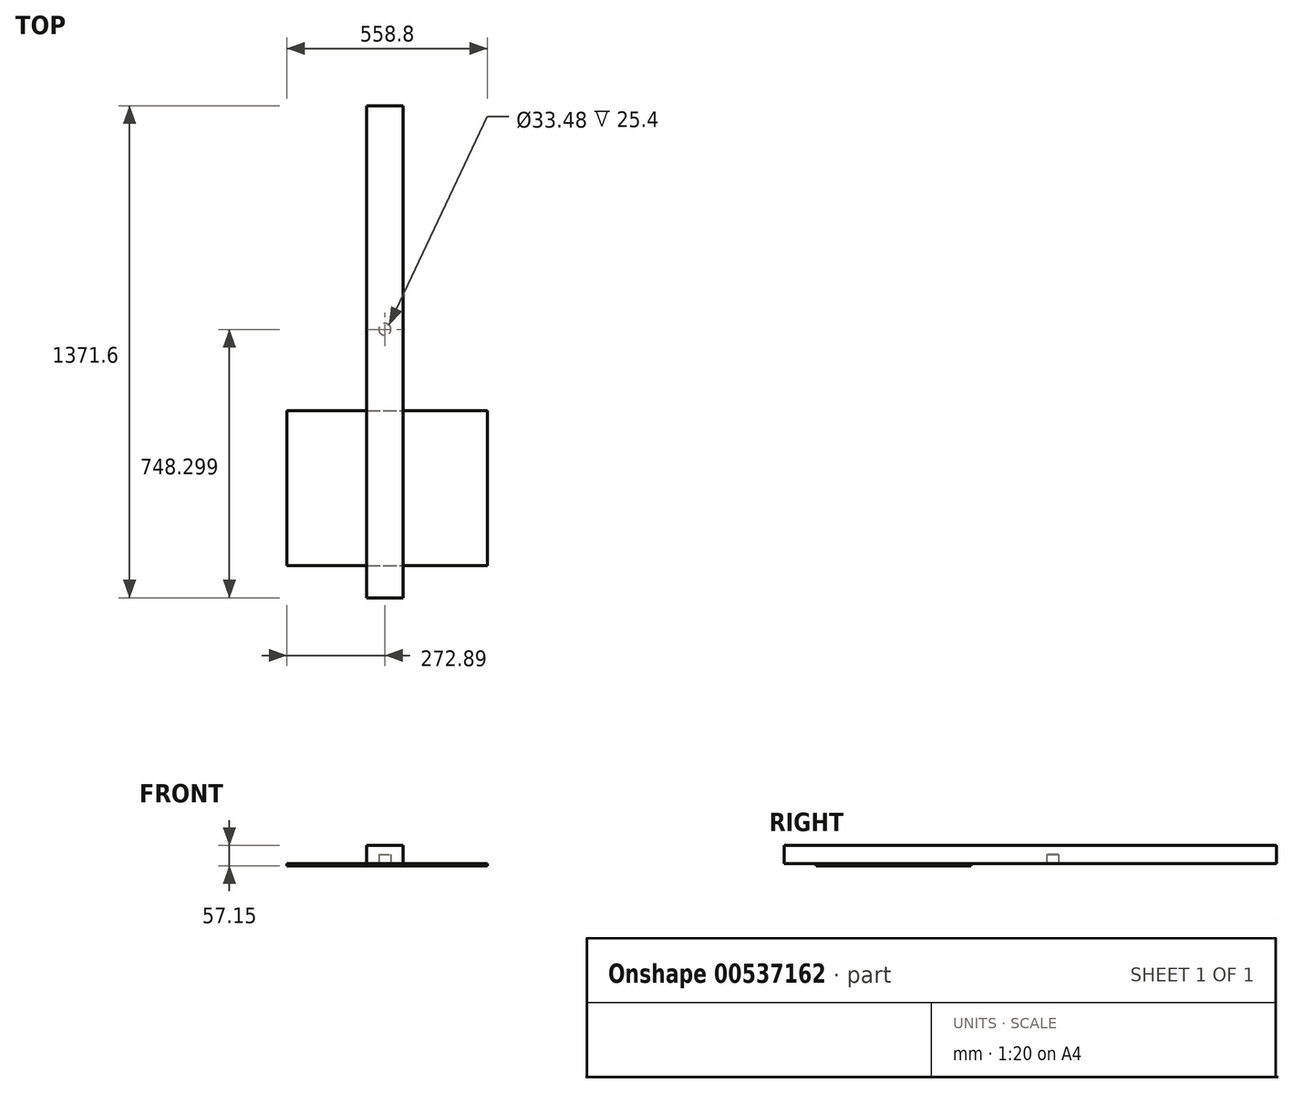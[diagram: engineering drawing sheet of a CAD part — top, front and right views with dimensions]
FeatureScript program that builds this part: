
annotation { "Feature Type Name" : "Feature", "Feature Type Description" : "" }
export const myFeature = defineFeature(function(context is Context, id is Id, definition is map)
    precondition{}
    {
        {
            var Q0;
            Q0=qCreatedBy(makeId("Front.planeOp"),FACE);
            var sketch = newSketch(context, id + "F0", { "sketchPlane" : qUnion([Q0])});
            skLineSegment(sketch, "E0.bottom", {"start": v(-61.5, -24.62) * mm, "end": v(40.1, -24.62) * mm});
            skLineSegment(sketch, "E0.top", {"start": v(-61.5, 26.18) * mm, "end": v(40.1, 26.18) * mm});
            skLineSegment(sketch, "E0.left", {"start": v(-61.5, -24.62) * mm, "end": v(-61.5, 26.18) * mm});
            skLineSegment(sketch, "E0.right", {"start": v(40.1, -24.62) * mm, "end": v(40.1, 26.18) * mm});
            skSolve(sketch);
        }
        {
            var Q0;
            Q0 = qSketchRegion(id + "F0", true);
            extrude(context, id + "F1", {"entities" : qUnion([Q0]), "depth" : 1371.6 * mm, "offsetDistance" : 25.4 * mm});
        }
        {
            var Q0;
            Q0=makeQuery(id+"F1.opExtrude","SWEPT_FACE",FACE,{"disambiguationData":[OSD([sQuery(id+"F0.wireOp",EDGE,"E0.bottom")])]});
            var sketch = newSketch(context, id + "F2", { "sketchPlane" : qUnion([Q0])});
            skCircle(sketch, "E1", {"center": v(-10.77, 623.3) * mm, "radius": 16.74 * mm});
            skSolve(sketch);
        }
        {
            var Q0;
            Q0 = qSketchRegion(id + "F2", true);
            extrude(context, id + "F3", {"entities" : qUnion([Q0]), "operationType" : NewBodyOperationType.REMOVE, "oppositeDirection" : true, "depth" : 25.4 * mm, "offsetDistance" : 25.4 * mm});
        }
        {
            var Q0;
            Q0=makeQuery(id+"F1.opExtrude","SWEPT_FACE",FACE,{"disambiguationData":[OSD([sQuery(id+"F0.wireOp",EDGE,"E0.bottom")])]});
            var sketch = newSketch(context, id + "F4", { "sketchPlane" : qUnion([Q0])});
            skLineSegment(sketch, "E2.bottom", {"start": v(-283.66, 1281.97) * mm, "end": v(275.14, 1281.97) * mm});
            skLineSegment(sketch, "E2.top", {"start": v(-283.66, 850.17) * mm, "end": v(275.14, 850.17) * mm});
            skLineSegment(sketch, "E2.left", {"start": v(-283.66, 1281.97) * mm, "end": v(-283.66, 850.17) * mm});
            skLineSegment(sketch, "E2.right", {"start": v(275.14, 1281.97) * mm, "end": v(275.14, 850.17) * mm});
            skSolve(sketch);
        }
        {
            var Q0;
            Q0 = qSketchRegion(id + "F4", true);
            extrude(context, id + "F5", {"entities" : qUnion([Q0]), "operationType" : NewBodyOperationType.ADD, "depth" : 6.35 * mm, "offsetDistance" : 25.4 * mm});
        }
    });
